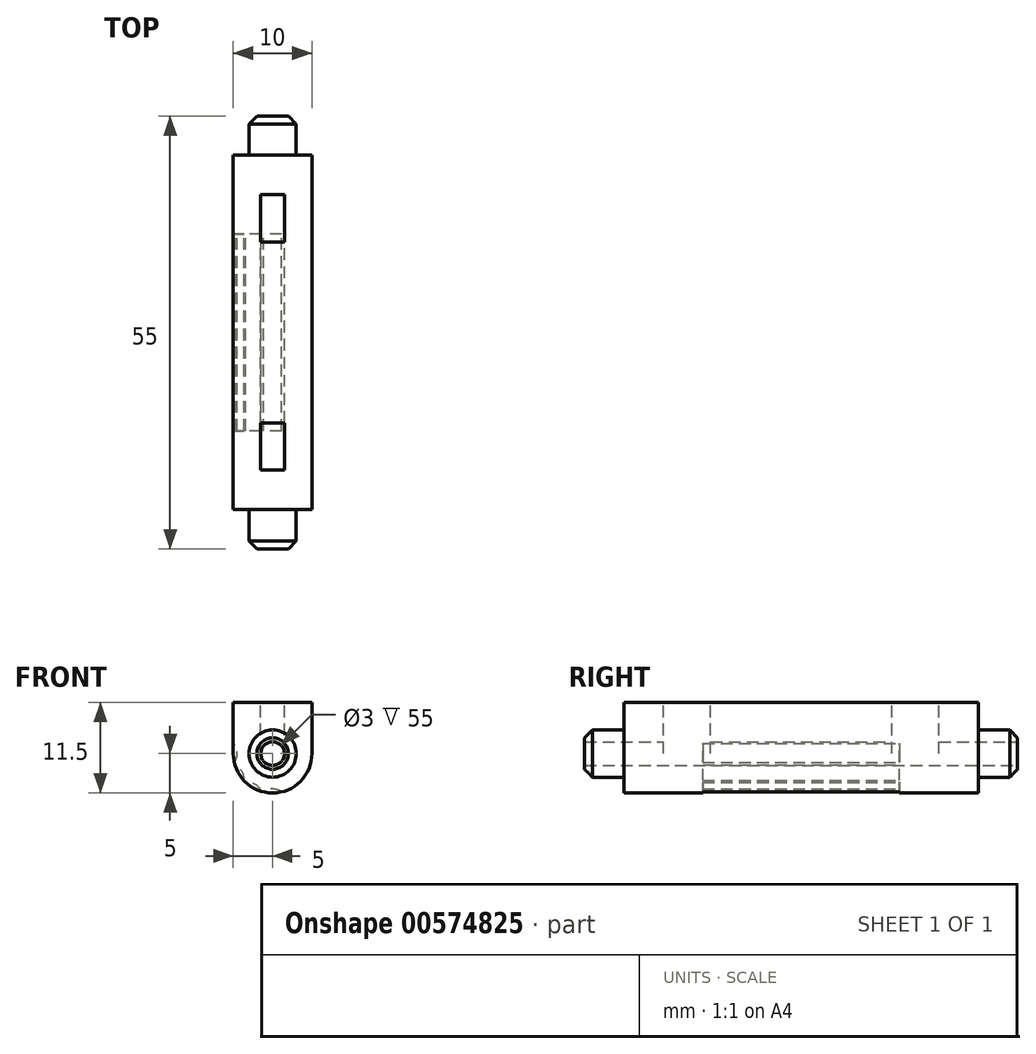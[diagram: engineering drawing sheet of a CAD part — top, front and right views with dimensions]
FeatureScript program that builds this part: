
annotation { "Feature Type Name" : "Feature", "Feature Type Description" : "" }
export const myFeature = defineFeature(function(context is Context, id is Id, definition is map)
    precondition{}
    {
        {
            var Q0;
            Q0=qCreatedBy(makeId("Front.planeOp"),FACE);
            var sketch = newSketch(context, id + "F0", { "sketchPlane" : qUnion([Q0])});
            skLineSegment(sketch, "E0.right", {"start": v(5, 6.5) * mm, "end": v(5, 0) * mm});
            skArc(sketch, "E1", {"start": v(-5, 0) * mm, "mid": v(0, -5) * mm, "end": v(5, 0) * mm});
            skPoint(sketch, "E2.oppositeSnap0", {"position": v(0, -5) * mm});
            skLineSegment(sketch, "E2.bottom", {"start": v(5, 6.5) * mm, "end": v(-5, 6.5) * mm});
            skLineSegment(sketch, "E2.right", {"start": v(-5, 6.5) * mm, "end": v(-5, 0) * mm});
            skPoint(sketch, "E3.orphan", {"position": v(-5, 0) * mm});
            skLineSegment(sketch, "E4", {"start": v(0, 0) * mm, "end": v(-5.63, -3.25) * mm, "construction": true});
            skArc(sketch, "E5", {"start": v(0, -6.5) * mm, "mid": v(-4.6, -4.6) * mm, "end": v(-6.5, 0) * mm, "construction": true});
            skLineSegment(sketch, "E6", {"start": v(0, 0) * mm, "end": v(-3.25, -5.63) * mm, "construction": true});
            skArc(sketch, "E7", {"start": v(1.15, -4.87) * mm, "mid": v(0, -4.5) * mm, "end": v(-1.15, -4.87) * mm});
            skArc(sketch, "E8", {"start": v(-1.43, -4.79) * mm, "mid": v(-2.25, -3.9) * mm, "end": v(-3.43, -3.64) * mm});
            skArc(sketch, "E9", {"start": v(-3.64, -3.43) * mm, "mid": v(-3.9, -2.25) * mm, "end": v(-4.79, -1.43) * mm});
            skArc(sketch, "E10", {"start": v(-4.87, -1.15) * mm, "mid": v(-4.5, 0.1) * mm, "end": v(-5, 1.32) * mm});
            skCircle(sketch, "E11", {"center": v(0, 0) * mm, "radius": 3 * mm});
            skCircle(sketch, "E12", {"center": v(0, 0) * mm, "radius": 1.5 * mm});
            skSolve(sketch);
        }
        {
            var Q0;
            Q0=makeQuery(id+"F0.imprint","IMPRINT",FACE,{"disambiguationData":[TD([[makeQuery(id+"F0.imprint","IMPRINT",EDGE,{"derivedFrom":sQuery(id+"F0.wireOp",EDGE,"E0.right")}),-1.0]])]});
            var Q1;
            Q1=makeQuery(id+"F0.imprint","IMPRINT",FACE,{"disambiguationData":[TD([[makeQuery(id+"F0.imprint","IMPRINT",EDGE,{"derivedFrom":sQuery(id+"F0.wireOp",EDGE,"E11")}),1.0]])]});
            extrude(context, id + "F1", {"entities" : qUnion([Q0, Q1]), "depth" : 22.5 * mm});
        }
        {
            var Q0;
            {var subQ3=sQuery(id+"F0.wireOp",EDGE,"E10");Q0=makeQuery(id+"F0.imprint","IMPRINT",FACE,{"disambiguationData":[TD([[makeQuery(id+"F0.imprint","IMPRINT",EDGE,{"derivedFrom":subQ3}),1.0]])]});}
            var Q1;
            {var subQ0=sQuery(id+"F0.wireOp",EDGE,"E9");Q1=makeQuery(id+"F0.imprint","IMPRINT",FACE,{"disambiguationData":[TD([[makeQuery(id+"F0.imprint","IMPRINT",EDGE,{"derivedFrom":subQ0}),1.0]])]});}
            var Q2;
            {var subQ0=sQuery(id+"F0.wireOp",EDGE,"E8");Q2=makeQuery(id+"F0.imprint","IMPRINT",FACE,{"disambiguationData":[TD([[makeQuery(id+"F0.imprint","IMPRINT",EDGE,{"derivedFrom":subQ0}),1.0]])]});}
            var Q3;
            {var subQ0=sQuery(id+"F0.wireOp",EDGE,"E7");Q3=makeQuery(id+"F0.imprint","IMPRINT",FACE,{"disambiguationData":[TD([[makeQuery(id+"F0.imprint","IMPRINT",EDGE,{"derivedFrom":subQ0}),1.0]])]});}
            extrude(context, id + "F2", {"entities" : qUnion([Q0, Q1, Q2, Q3]), "operationType" : NewBodyOperationType.ADD, "depth" : 10 * mm});
        }
        {
            var Q0;
            {var subQ6=sQuery(id+"F0.wireOp",EDGE,"E0.right");Q0=makeQuery(id+"F0.imprint","IMPRINT",FACE,{"disambiguationData":[TD([[makeQuery(id+"F0.imprint","IMPRINT",EDGE,{"derivedFrom":subQ6}),-1.0]])]});}
            var sketch = newSketch(context, id + "F3", { "sketchPlane" : qUnion([Q0])});
            skCircle(sketch, "E13", {"center": v(0, 0) * mm, "radius": 3 * mm});
            skCircle(sketch, "E14", {"center": v(0, 0) * mm, "radius": 1.5 * mm});
            skSolve(sketch);
        }
        {
            var Q0;
            Q0=makeQuery(id+"F3.imprint","IMPRINT",FACE,{"disambiguationData":[TD([[makeQuery(id+"F3.imprint","IMPRINT",EDGE,{"derivedFrom":sQuery(id+"F3.wireOp",EDGE,"E13")}),1.0]])]});
            extrude(context, id + "F4", {"entities" : qUnion([Q0]), "operationType" : NewBodyOperationType.ADD, "oppositeDirection" : true, "depth" : 5 * mm});
        }
        {
            var Q0;
            Q0=makeQuery(id+"F4.opExtrude","CAP_EDGE",EDGE,{"disambiguationData":[OSD([sQuery(id+"F3.wireOp",EDGE,"E13")])],"isStart":false});
            chamfer(context, id + "F5", {"entities" : qUnion([Q0]), "width" : 1 * mm, "tangentPropagation" : true});
        }
        {
            var Q0;
            {var subQ0=makeQuery(id+"F1.opExtrude","SWEPT_FACE",FACE,{"disambiguationData":[OSD([sQuery(id+"F0.wireOp",EDGE,"E2.bottom")])]});Q0=makeQuery(id+"F8.boolean.opBoolean","MERGE",FACE,{"derivedFrom":[subQ0,makeQuery(id+"F8.opPattern","COPY",FACE,{"derivedFrom":subQ0,"instanceName":"1"})]});}
            var sketch = newSketch(context, id + "F6", { "sketchPlane" : qUnion([Q0])});
            skLineSegment(sketch, "E15.bottom", {"start": v(-1.5, -5) * mm, "end": v(1.5, -5) * mm});
            skLineSegment(sketch, "E15.top", {"start": v(-1.5, -11) * mm, "end": v(1.5, -11) * mm});
            skLineSegment(sketch, "E15.left", {"start": v(-1.5, -5) * mm, "end": v(-1.5, -11) * mm});
            skLineSegment(sketch, "E15.right", {"start": v(1.5, -5) * mm, "end": v(1.5, -11) * mm});
            skSolve(sketch);
        }
        {
            var Q0;
            Q0=makeQuery(id+"F6.imprint","IMPRINT",FACE,{"disambiguationData":[TD([[makeQuery(id+"F6.imprint","IMPRINT",EDGE,{"derivedFrom":sQuery(id+"F6.wireOp",EDGE,"E15.bottom")}),-1.0]])]});
            var Q1;
            Q1=qCreatedBy(makeId("Top.planeOp"),FACE);
            extrude(context, id + "F7", {"entities" : qUnion([Q0]), "operationType" : NewBodyOperationType.REMOVE, "endBound" : BoundingType.UP_TO_SURFACE, "oppositeDirection" : true, "endBoundEntityFace" : qUnion([Q1]), "depth" : 25 * mm});
        }
        {
            var Q0;
            Q0=makeQuery(id+"F1.opExtrude","SWEPT_BODY",BODY,{"disambiguationData":[OSD([sQuery(id+"F0.wireOp",EDGE,"E0.right"),sQuery(id+"F0.wireOp",EDGE,"E1"),sQuery(id+"F0.wireOp",EDGE,"E2.bottom"),sQuery(id+"F0.wireOp",EDGE,"E2.right"),sQuery(id+"F0.wireOp",EDGE,"E7"),sQuery(id+"F0.wireOp",EDGE,"E8"),sQuery(id+"F0.wireOp",EDGE,"E9"),sQuery(id+"F0.wireOp",EDGE,"E10"),sQuery(id+"F0.wireOp",EDGE,"E12")])]});
            var Q1;
            Q1=makeQuery(id+"F1.opExtrude","CAP_FACE",FACE,{"disambiguationData":[OSD([sQuery(id+"F0.wireOp",EDGE,"E0.bottom"),sQuery(id+"F0.wireOp",EDGE,"E0.left"),sQuery(id+"F0.wireOp",EDGE,"E0.right"),sQuery(id+"F0.wireOp",EDGE,"E1")])],"isStart":false});
            mirror(context, id + "F8", {"operationType" : NewBodyOperationType.ADD, "entities" : qUnion([Q0]), "mirrorPlane" : qUnion([Q1])});
        }
    });
